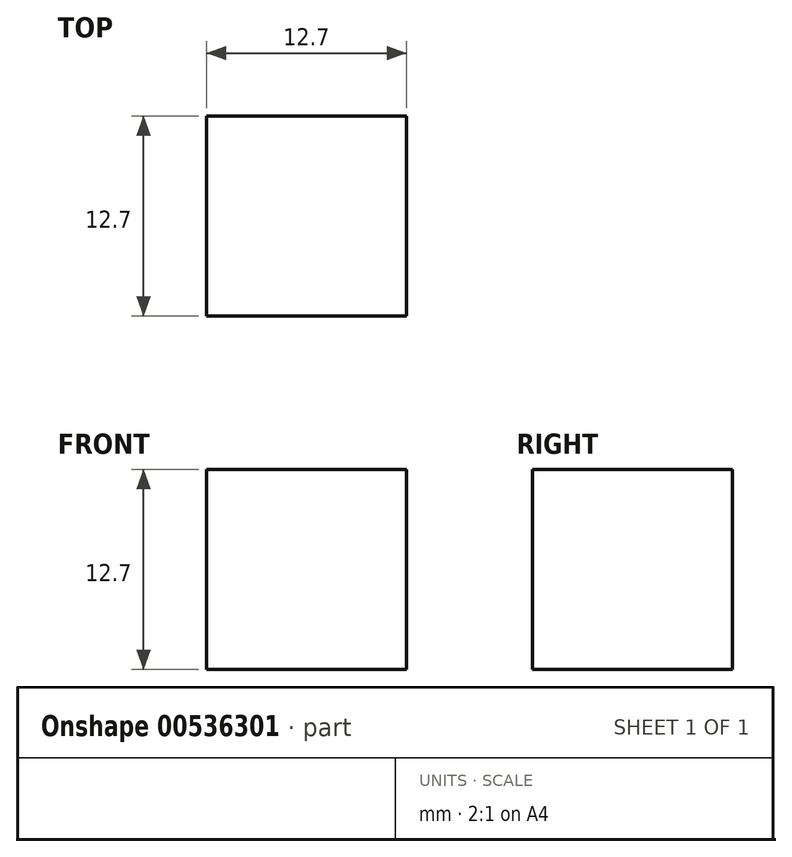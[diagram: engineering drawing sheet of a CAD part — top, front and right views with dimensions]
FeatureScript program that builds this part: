
annotation { "Feature Type Name" : "Feature", "Feature Type Description" : "" }
export const myFeature = defineFeature(function(context is Context, id is Id, definition is map)
    precondition{}
    {
        {
            var Q0;
            Q0=qCreatedBy(makeId("Front.planeOp"),FACE);
            var sketch = newSketch(context, id + "F0", { "sketchPlane" : qUnion([Q0])});
            skLineSegment(sketch, "E0.bottom", {"start": v(-18.57, -4.04) * mm, "end": v(-5.87, -4.04) * mm});
            skLineSegment(sketch, "E0.top", {"start": v(-18.57, -16.74) * mm, "end": v(-5.87, -16.74) * mm});
            skLineSegment(sketch, "E0.left", {"start": v(-18.57, -4.04) * mm, "end": v(-18.57, -16.74) * mm});
            skLineSegment(sketch, "E0.right", {"start": v(-5.87, -4.04) * mm, "end": v(-5.87, -16.74) * mm});
            skSolve(sketch);
        }
        {
            var Q0;
            Q0=makeQuery(id+"F0.imprint","IMPRINT",FACE,{"disambiguationData":[TD([[makeQuery(id+"F0.imprint","IMPRINT",EDGE,{"derivedFrom":sQuery(id+"F0.wireOp",EDGE,"E0.bottom")}),-1.0]])]});
            extrude(context, id + "F1", {"entities" : qUnion([Q0]), "depth" : 12.7 * mm, "offsetDistance" : 25.4 * mm});
        }
    });
